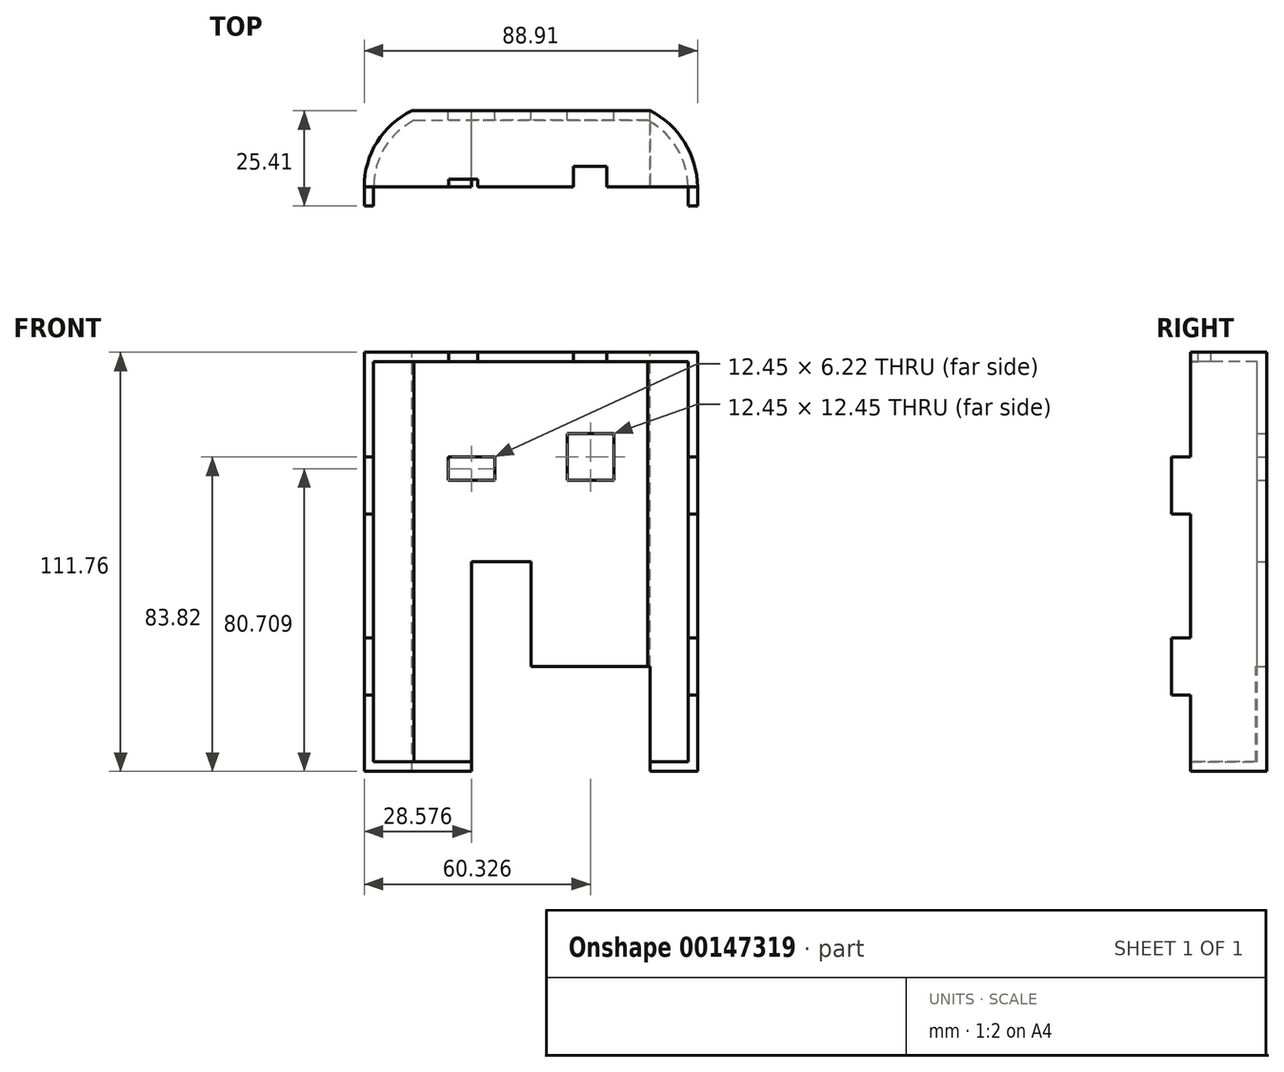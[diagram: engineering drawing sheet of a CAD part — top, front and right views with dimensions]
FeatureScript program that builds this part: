
annotation { "Feature Type Name" : "Feature", "Feature Type Description" : "" }
export const myFeature = defineFeature(function(context is Context, id is Id, definition is map)
    precondition{}
    {
        {
            var Q0;
            Q0=qCreatedBy(makeId("Top.planeOp"),FACE);
            var sketch = newSketch(context, id + "F0", { "sketchPlane" : qUnion([Q0])});
            skLineSegment(sketch, "E0.bottom", {"start": v(-8.58, 19.44) * mm, "end": v(54.92, 19.44) * mm});
            skLineSegment(sketch, "E1", {"start": v(67.63, -0.89) * mm, "end": v(-21.28, -0.89) * mm});
            skArc(sketch, "E2", {"start": v(-8.58, 19.44) * mm, "mid": v(-17.85, 11.1) * mm, "end": v(-21.28, -0.89) * mm});
            skArc(sketch, "E3", {"start": v(67.63, -0.89) * mm, "mid": v(64.16, 11.08) * mm, "end": v(54.92, 19.44) * mm});
            skLineSegment(sketch, "E4", {"start": v(1.33, -0.88) * mm, "end": v(1.33, 1.2) * mm});
            skLineSegment(sketch, "E5", {"start": v(1.33, 1.2) * mm, "end": v(9.07, 1.2) * mm});
            skLineSegment(sketch, "E6", {"start": v(9.07, 1.2) * mm, "end": v(9.07, -0.89) * mm});
            skLineSegment(sketch, "E7", {"start": v(34.47, -0.89) * mm, "end": v(34.47, 4.57) * mm});
            skLineSegment(sketch, "E8", {"start": v(34.47, 4.57) * mm, "end": v(43.41, 4.57) * mm});
            skLineSegment(sketch, "E9", {"start": v(43.41, 4.57) * mm, "end": v(43.41, -0.89) * mm});
            skSolve(sketch);
        }
        {
            var Q0;
            Q0=makeQuery(id+"F0.imprint","IMPRINT",FACE,{"disambiguationData":[TD([[makeQuery(id+"F0.imprint","IMPRINT",EDGE,{"derivedFrom":sQuery(id+"F0.wireOp",EDGE,"E0.bottom")}),-1.0]])]});
            var Q1;
            {var subQ0=sQuery(id+"F0.wireOp",EDGE,"E7");Q1=makeQuery(id+"F0.imprint","IMPRINT",FACE,{"disambiguationData":[TD([[makeQuery(id+"F0.imprint","IMPRINT",EDGE,{"derivedFrom":subQ0}),-1.0]])]});}
            extrude(context, id + "F1", {"entities" : qUnion([Q0, Q1]), "oppositeDirection" : true, "depth" : 111.76 * mm});
        }
        {
            var Q0;
            Q0=makeQuery(id+"F1.opExtrude","SWEPT_FACE",FACE,{"disambiguationData":[OSD([sQuery(id+"F0.wireOp",EDGE,"E1")])]});
            shell(context, id + "F2", {"entities" : qUnion([Q0]), "thickness" : 2.54 * mm});
        }
        {
            var Q0;
            Q0=makeQuery(id+"F0.imprint","IMPRINT",FACE,{"disambiguationData":[TD([[makeQuery(id+"F0.imprint","IMPRINT",EDGE,{"derivedFrom":sQuery(id+"F0.wireOp",EDGE,"E0.bottom")}),-1.0]])]});
            var sketch = newSketch(context, id + "F3", { "sketchPlane" : qUnion([Q0])});
            skLineSegment(sketch, "E10.bottom", {"start": v(1.31, -0.89) * mm, "end": v(9.06, -0.89) * mm});
            skLineSegment(sketch, "E10.top", {"start": v(1.31, 1.2) * mm, "end": v(9.06, 1.2) * mm});
            skLineSegment(sketch, "E10.left", {"start": v(1.31, -0.89) * mm, "end": v(1.31, 1.2) * mm});
            skLineSegment(sketch, "E10.right", {"start": v(9.06, -0.89) * mm, "end": v(9.06, 1.2) * mm});
            skLineSegment(sketch, "E11.bottom", {"start": v(34.46, -0.88) * mm, "end": v(43.4, -0.88) * mm});
            skLineSegment(sketch, "E11.top", {"start": v(34.46, 4.58) * mm, "end": v(43.4, 4.58) * mm});
            skLineSegment(sketch, "E11.left", {"start": v(34.46, -0.88) * mm, "end": v(34.46, 4.58) * mm});
            skLineSegment(sketch, "E11.right", {"start": v(43.4, -0.88) * mm, "end": v(43.4, 4.58) * mm});
            skSolve(sketch);
        }
        {
            var Q0;
            {var subQ0=sQuery(id+"F3.wireOp",EDGE,"E10.top");Q0=makeQuery(id+"F3.imprint","IMPRINT",FACE,{"disambiguationData":[TD([[makeQuery(id+"F3.imprint","IMPRINT",EDGE,{"derivedFrom":subQ0}),-1.0]])]});}
            extrude(context, id + "F4", {"entities" : qUnion([Q0]), "operationType" : NewBodyOperationType.REMOVE, "oppositeDirection" : true, "depth" : 25.4 * mm});
        }
        {
            var Q0;
            {var subQ0=sQuery(id+"F0.wireOp",EDGE,"E7");Q0=makeQuery(id+"F0.imprint","IMPRINT",FACE,{"disambiguationData":[TD([[makeQuery(id+"F0.imprint","IMPRINT",EDGE,{"derivedFrom":subQ0}),-1.0]])]});}
            extrude(context, id + "F5", {"entities" : qUnion([Q0]), "operationType" : NewBodyOperationType.REMOVE, "oppositeDirection" : true, "depth" : 25.4 * mm});
        }
        {
            var Q0;
            Q0=makeQuery(id+"F1.opExtrude","CAP_FACE",FACE,{"disambiguationData":[OSD([sQuery(id+"F0.wireOp",EDGE,"E0.bottom"),sQuery(id+"F0.wireOp",EDGE,"E1"),sQuery(id+"F0.wireOp",EDGE,"E2"),sQuery(id+"F0.wireOp",EDGE,"E3")])],"isStart":false});
            var sketch = newSketch(context, id + "F6", { "sketchPlane" : qUnion([Q0])});
            skPoint(sketch, "E12", {"position": v(23.17, 0.89) * mm});
            skArc(sketch, "E13", {"start": v(17.33, 0.89) * mm, "mid": v(23.17, -4.96) * mm, "end": v(29.02, 0.89) * mm});
            skSolve(sketch);
        }
        {
            var Q0;
            {var subQ0=sQuery(id+"F6.wireOp",EDGE,"E13");Q0=makeQuery(id+"F6.imprint","IMPRINT",FACE,{"disambiguationData":[TD([[makeQuery(id+"F6.imprint","IMPRINT",EDGE,{"derivedFrom":subQ0}),1.0]])]});}
            extrude(context, id + "F7", {"entities" : qUnion([Q0]), "operationType" : NewBodyOperationType.REMOVE, "oppositeDirection" : true, "depth" : 25.4 * mm});
        }
        {
            var Q0;
            {var subQ0=sQuery(id+"F0.wireOp",EDGE,"E3");var subQ1=sQuery(id+"F0.wireOp",EDGE,"E2");var subQ2=sQuery(id+"F0.wireOp",EDGE,"E1");var subQ6=makeQuery(id+"F1.opExtrude","SWEPT_FACE",FACE,{"disambiguationData":[OSD([subQ0])]});Q0=makeQuery(id+"F7.boolean.opBoolean","SPLIT",FACE,{"disambiguationData":[TD([subQ6])],"derivedFrom":makeQuery(id+"F5.boolean.opBoolean","SPLIT",FACE,{"disambiguationData":[TD([makeQuery(id+"F1.opExtrude","SWEPT_FACE",FACE,{"disambiguationData":[OSD([subQ1])]})])],"derivedFrom":makeQuery(id+"F1.opExtrude","SWEPT_FACE",FACE,{"disambiguationData":[OSD([subQ2])]})})});}
            var sketch = newSketch(context, id + "F8", { "sketchPlane" : qUnion([Q0])});
            skLineSegment(sketch, "E14", {"start": v(67.63, 0) * mm, "end": v(67.63, -111.76) * mm});
            skLineSegment(sketch, "E15", {"start": v(67.63, -55.88) * mm, "end": v(67.63, 0) * mm});
            skLineSegment(sketch, "E16", {"start": v(67.63, -55.88) * mm, "end": v(67.63, -111.76) * mm});
            skLineSegment(sketch, "E17", {"start": v(67.63, -27.94) * mm, "end": v(65.09, -27.94) * mm});
            skLineSegment(sketch, "E18", {"start": v(67.63, -83.82) * mm, "end": v(65.09, -83.82) * mm});
            skLineSegment(sketch, "E19.top", {"start": v(67.63, -76.2) * mm, "end": v(65.09, -76.2) * mm});
            skLineSegment(sketch, "E19.left", {"start": v(67.63, -83.82) * mm, "end": v(67.63, -76.2) * mm});
            skLineSegment(sketch, "E19.right", {"start": v(65.09, -83.82) * mm, "end": v(65.09, -76.2) * mm});
            skLineSegment(sketch, "E20.top", {"start": v(67.63, -91.44) * mm, "end": v(65.09, -91.44) * mm});
            skLineSegment(sketch, "E20.left", {"start": v(67.63, -83.82) * mm, "end": v(67.63, -91.44) * mm});
            skLineSegment(sketch, "E20.right", {"start": v(65.09, -83.82) * mm, "end": v(65.09, -91.44) * mm});
            skLineSegment(sketch, "E21.top", {"start": v(67.63, -35.56) * mm, "end": v(65.09, -35.56) * mm});
            skLineSegment(sketch, "E21.left", {"start": v(67.63, -27.94) * mm, "end": v(67.63, -35.56) * mm});
            skLineSegment(sketch, "E21.right", {"start": v(65.09, -27.94) * mm, "end": v(65.09, -35.56) * mm});
            skLineSegment(sketch, "E22.top", {"start": v(67.63, -43.18) * mm, "end": v(65.09, -43.18) * mm});
            skLineSegment(sketch, "E22.left", {"start": v(67.63, -35.56) * mm, "end": v(67.63, -43.18) * mm});
            skLineSegment(sketch, "E22.right", {"start": v(65.09, -35.56) * mm, "end": v(65.09, -43.18) * mm});
            skSolve(sketch);
        }
        {
            var Q0;
            Q0=makeQuery(id+"F8.imprint","IMPRINT",FACE,{"disambiguationData":[TD([[makeQuery(id+"F8.imprint","IMPRINT",EDGE,{"derivedFrom":sQuery(id+"F8.wireOp",EDGE,"E17")}),1.0]])]});
            var Q1;
            Q1=makeQuery(id+"F8.imprint","IMPRINT",FACE,{"disambiguationData":[TD([[makeQuery(id+"F8.imprint","IMPRINT",EDGE,{"derivedFrom":sQuery(id+"F8.wireOp",EDGE,"E21.top")}),1.0]])]});
            var Q2;
            Q2=makeQuery(id+"F8.imprint","IMPRINT",FACE,{"disambiguationData":[TD([[makeQuery(id+"F8.imprint","IMPRINT",EDGE,{"derivedFrom":sQuery(id+"F8.wireOp",EDGE,"E19.top")}),1.0]])]});
            var Q3;
            Q3=makeQuery(id+"F8.imprint","IMPRINT",FACE,{"disambiguationData":[TD([[makeQuery(id+"F8.imprint","IMPRINT",EDGE,{"derivedFrom":sQuery(id+"F8.wireOp",EDGE,"E18")}),1.0]])]});
            extrude(context, id + "F9", {"entities" : qUnion([Q0, Q1, Q2, Q3]), "operationType" : NewBodyOperationType.ADD, "depth" : 5.08 * mm});
        }
        {
            var Q0;
            {var subQ1=sQuery(id+"F0.wireOp",EDGE,"E2");var subQ2=sQuery(id+"F0.wireOp",EDGE,"E1");var subQ6=makeQuery(id+"F1.opExtrude","SWEPT_FACE",FACE,{"disambiguationData":[OSD([subQ1])]});Q0=makeQuery(id+"F7.boolean.opBoolean","SPLIT",FACE,{"disambiguationData":[TD([subQ6])],"derivedFrom":makeQuery(id+"F5.boolean.opBoolean","SPLIT",FACE,{"disambiguationData":[TD([subQ6])],"derivedFrom":makeQuery(id+"F1.opExtrude","SWEPT_FACE",FACE,{"disambiguationData":[OSD([subQ2])]})})});}
            var sketch = newSketch(context, id + "F10", { "sketchPlane" : qUnion([Q0])});
            skLineSegment(sketch, "E23", {"start": v(-21.28, 0) * mm, "end": v(-21.28, -111.76) * mm});
            skLineSegment(sketch, "E24", {"start": v(-21.28, -111.76) * mm, "end": v(-21.28, -55.88) * mm});
            skLineSegment(sketch, "E25", {"start": v(-21.28, -55.88) * mm, "end": v(-21.28, 0) * mm});
            skLineSegment(sketch, "E26", {"start": v(-21.28, -27.94) * mm, "end": v(-18.74, -27.94) * mm});
            skPoint(sketch, "E26.endSnap0", {"position": v(-18.74, -55.88) * mm});
            skLineSegment(sketch, "E27", {"start": v(-21.28, -83.82) * mm, "end": v(-18.74, -83.82) * mm});
            skLineSegment(sketch, "E28.top", {"start": v(-21.28, -43.18) * mm, "end": v(-18.74, -43.18) * mm});
            skLineSegment(sketch, "E28.left", {"start": v(-21.28, -27.94) * mm, "end": v(-21.28, -43.18) * mm});
            skLineSegment(sketch, "E28.right", {"start": v(-18.74, -27.94) * mm, "end": v(-18.74, -43.18) * mm});
            skLineSegment(sketch, "E29.top", {"start": v(-21.28, -76.2) * mm, "end": v(-18.74, -76.2) * mm});
            skLineSegment(sketch, "E29.left", {"start": v(-21.28, -83.82) * mm, "end": v(-21.28, -76.2) * mm});
            skLineSegment(sketch, "E29.right", {"start": v(-18.74, -83.82) * mm, "end": v(-18.74, -76.2) * mm});
            skLineSegment(sketch, "E30.top", {"start": v(-21.28, -91.44) * mm, "end": v(-18.74, -91.44) * mm});
            skLineSegment(sketch, "E30.left", {"start": v(-21.28, -83.82) * mm, "end": v(-21.28, -91.44) * mm});
            skLineSegment(sketch, "E30.right", {"start": v(-18.74, -83.82) * mm, "end": v(-18.74, -91.44) * mm});
            skSolve(sketch);
        }
        {
            var Q0;
            Q0=makeQuery(id+"F10.imprint","IMPRINT",FACE,{"disambiguationData":[TD([[makeQuery(id+"F10.imprint","IMPRINT",EDGE,{"derivedFrom":sQuery(id+"F10.wireOp",EDGE,"E26")}),-1.0]])]});
            var Q1;
            Q1=makeQuery(id+"F10.imprint","IMPRINT",FACE,{"disambiguationData":[TD([[makeQuery(id+"F10.imprint","IMPRINT",EDGE,{"derivedFrom":sQuery(id+"F10.wireOp",EDGE,"E29.top")}),-1.0]])]});
            var Q2;
            Q2=makeQuery(id+"F10.imprint","IMPRINT",FACE,{"disambiguationData":[TD([[makeQuery(id+"F10.imprint","IMPRINT",EDGE,{"derivedFrom":sQuery(id+"F10.wireOp",EDGE,"E27")}),-1.0]])]});
            extrude(context, id + "F11", {"entities" : qUnion([Q0, Q1, Q2]), "operationType" : NewBodyOperationType.ADD, "depth" : 5.08 * mm});
        }
        {
            var Q0;
            Q0=makeQuery(id+"F1.opExtrude","SWEPT_FACE",FACE,{"disambiguationData":[OSD([sQuery(id+"F0.wireOp",EDGE,"E0.bottom")])]});
            var sketch = newSketch(context, id + "F12", { "sketchPlane" : qUnion([Q0])});
            skLineSegment(sketch, "E31", {"start": v(-23.17, 0) * mm, "end": v(-23.17, -111.76) * mm});
            skLineSegment(sketch, "E32", {"start": v(8.58, -55.88) * mm, "end": v(-54.92, -55.88) * mm});
            skLineSegment(sketch, "E33", {"start": v(8.58, -55.88) * mm, "end": v(8.58, 0) * mm});
            skLineSegment(sketch, "E34", {"start": v(8.58, 0) * mm, "end": v(-23.17, 0) * mm});
            skLineSegment(sketch, "E35", {"start": v(-23.17, 0) * mm, "end": v(-54.92, 0) * mm});
            skLineSegment(sketch, "E36", {"start": v(-54.92, 0) * mm, "end": v(-54.92, -55.88) * mm});
            skLineSegment(sketch, "E37", {"start": v(-54.92, -55.88) * mm, "end": v(-54.92, -111.76) * mm});
            skLineSegment(sketch, "E38", {"start": v(-54.92, -111.76) * mm, "end": v(-23.17, -111.76) * mm});
            skLineSegment(sketch, "E39", {"start": v(-23.17, -111.76) * mm, "end": v(8.58, -111.76) * mm});
            skLineSegment(sketch, "E40", {"start": v(8.58, -111.76) * mm, "end": v(8.58, -55.88) * mm});
            skLineSegment(sketch, "E41", {"start": v(8.58, -83.82) * mm, "end": v(-23.17, -83.82) * mm});
            skLineSegment(sketch, "E42", {"start": v(-23.17, -55.88) * mm, "end": v(8.58, -55.88) * mm});
            skLineSegment(sketch, "E43", {"start": v(-23.17, -55.88) * mm, "end": v(-54.92, -55.88) * mm});
            skLineSegment(sketch, "E44", {"start": v(-7.3, -55.88) * mm, "end": v(-7.3, -111.76) * mm});
            skLineSegment(sketch, "E45", {"start": v(-7.3, -55.88) * mm, "end": v(-7.3, 0) * mm});
            skLineSegment(sketch, "E46", {"start": v(8.58, -27.94) * mm, "end": v(-23.17, -27.94) * mm});
            skPoint(sketch, "E46.endSnap0", {"position": v(-7.3, -27.94) * mm});
            skLineSegment(sketch, "E47", {"start": v(-23.17, -27.94) * mm, "end": v(-54.92, -27.94) * mm});
            skLineSegment(sketch, "E48", {"start": v(-39.05, 0) * mm, "end": v(-39.05, -111.76) * mm});
            skLineSegment(sketch, "E49", {"start": v(-23.17, -83.82) * mm, "end": v(-54.92, -83.82) * mm});
            skCircle(sketch, "E50", {"center": v(-7.3, -83.82) * mm, "radius": 4.45 * mm});
            skCircle(sketch, "E51", {"center": v(-39.05, -83.82) * mm, "radius": 4.45 * mm});
            skLineSegment(sketch, "E52", {"start": v(-7.3, -27.94) * mm, "end": v(-7.3, -21.72) * mm});
            skLineSegment(sketch, "E53", {"start": v(-7.3, -21.72) * mm, "end": v(-1.07, -21.72) * mm});
            skLineSegment(sketch, "E54", {"start": v(-1.07, -21.72) * mm, "end": v(-1.07, -27.94) * mm});
            skLineSegment(sketch, "E55.bottom", {"start": v(-1.07, -21.72) * mm, "end": v(-13.52, -21.72) * mm});
            skLineSegment(sketch, "E55.top", {"start": v(-1.07, -34.16) * mm, "end": v(-13.52, -34.16) * mm});
            skLineSegment(sketch, "E55.left", {"start": v(-1.07, -21.72) * mm, "end": v(-1.07, -34.16) * mm});
            skLineSegment(sketch, "E55.right", {"start": v(-13.52, -21.72) * mm, "end": v(-13.52, -34.16) * mm});
            skLineSegment(sketch, "E56.MirrorCS", {"start": v(-45.27, -21.72) * mm, "end": v(-32.82, -21.72) * mm});
            skLineSegment(sketch, "E57.MirrorCS", {"start": v(-32.82, -21.72) * mm, "end": v(-32.82, -34.16) * mm});
            skLineSegment(sketch, "E58.MirrorCS", {"start": v(-45.27, -34.16) * mm, "end": v(-32.82, -34.16) * mm});
            skLineSegment(sketch, "E59.MirrorCS", {"start": v(-45.27, -21.72) * mm, "end": v(-45.27, -34.16) * mm});
            skSolve(sketch);
        }
        {
            var Q0;
            {var subQ0=sQuery(id+"F12.wireOp",EDGE,"E52");Q0=makeQuery(id+"F12.imprint","IMPRINT",FACE,{"disambiguationData":[TD([[makeQuery(id+"F12.imprint","IMPRINT",EDGE,{"derivedFrom":subQ0}),-1.0]])]});}
            var Q1;
            {var subQ0=sQuery(id+"F12.wireOp",EDGE,"E52");Q1=makeQuery(id+"F12.imprint","IMPRINT",FACE,{"disambiguationData":[TD([[makeQuery(id+"F12.imprint","IMPRINT",EDGE,{"derivedFrom":subQ0}),1.0]])]});}
            var Q2;
            {var subQ3=sQuery(id+"F12.wireOp",EDGE,"E55.top");var subQ5=sQuery(id+"F12.wireOp",EDGE,"E55.right");var subQ6=makeQuery(id+"F12.imprint","INTERSECT",VERTEX,{"derivedFrom":[subQ3,subQ5]});Q2=makeQuery(id+"F12.imprint","IMPRINT",FACE,{"disambiguationData":[TD([[makeQuery(id+"F12.imprint","IMPRINT",EDGE,{"disambiguationData":[TD([[subQ6,1.0]])],"derivedFrom":subQ3}),-1.0]])]});}
            var Q3;
            {var subQ3=sQuery(id+"F12.wireOp",EDGE,"E55.top");var subQ5=sQuery(id+"F12.wireOp",EDGE,"E55.left");var subQ7=makeQuery(id+"F12.imprint","INTERSECT",VERTEX,{"derivedFrom":[subQ3,subQ5]});Q3=makeQuery(id+"F12.imprint","IMPRINT",FACE,{"disambiguationData":[TD([[makeQuery(id+"F12.imprint","IMPRINT",EDGE,{"disambiguationData":[TD([[subQ7,-1.0]])],"derivedFrom":subQ3}),-1.0]])]});}
            var Q4;
            {var subQ0=sQuery(id+"F12.wireOp",EDGE,"E57.MirrorCS");var subQ1=sQuery(id+"F12.wireOp",EDGE,"E47");var subQ2=makeQuery(id+"F12.imprint","INTERSECT",VERTEX,{"derivedFrom":[subQ1,subQ0]});Q4=makeQuery(id+"F12.imprint","IMPRINT",FACE,{"disambiguationData":[TD([[makeQuery(id+"F12.imprint","IMPRINT",EDGE,{"disambiguationData":[TD([[subQ2,-1.0]])],"derivedFrom":subQ1}),-1.0]])]});}
            var Q5;
            {var subQ0=sQuery(id+"F12.wireOp",EDGE,"E48");var subQ1=sQuery(id+"F12.wireOp",EDGE,"E47");var subQ2=makeQuery(id+"F12.imprint","INTERSECT",VERTEX,{"derivedFrom":[subQ1,subQ0]});Q5=makeQuery(id+"F12.imprint","IMPRINT",FACE,{"disambiguationData":[TD([[makeQuery(id+"F12.imprint","IMPRINT",EDGE,{"disambiguationData":[TD([[subQ2,-1.0]])],"derivedFrom":subQ1}),-1.0]])]});}
            var Q6;
            {var subQ0=sQuery(id+"F12.wireOp",EDGE,"E48");var subQ1=sQuery(id+"F12.wireOp",EDGE,"E47");var subQ2=makeQuery(id+"F12.imprint","INTERSECT",VERTEX,{"derivedFrom":[subQ1,subQ0]});Q6=makeQuery(id+"F12.imprint","IMPRINT",FACE,{"disambiguationData":[TD([[makeQuery(id+"F12.imprint","IMPRINT",EDGE,{"disambiguationData":[TD([[subQ2,-1.0]])],"derivedFrom":subQ1}),1.0]])]});}
            var Q7;
            {var subQ0=sQuery(id+"F12.wireOp",EDGE,"E57.MirrorCS");var subQ1=sQuery(id+"F12.wireOp",EDGE,"E47");var subQ2=makeQuery(id+"F12.imprint","INTERSECT",VERTEX,{"derivedFrom":[subQ1,subQ0]});Q7=makeQuery(id+"F12.imprint","IMPRINT",FACE,{"disambiguationData":[TD([[makeQuery(id+"F12.imprint","IMPRINT",EDGE,{"disambiguationData":[TD([[subQ2,-1.0]])],"derivedFrom":subQ1}),1.0]])]});}
            var Q8;
            {var subQ0=sQuery(id+"F12.wireOp",EDGE,"E51");var subQ1=sQuery(id+"F12.wireOp",EDGE,"E48");var subQ2=makeQuery(id+"F12.imprint","INTERSECT",VERTEX,{"disambiguationData":[OD(0.0)],"derivedFrom":[subQ1,subQ0]});Q8=makeQuery(id+"F12.imprint","IMPRINT",FACE,{"disambiguationData":[TD([[makeQuery(id+"F12.imprint","IMPRINT",EDGE,{"disambiguationData":[TD([[subQ2,-1.0]])],"derivedFrom":subQ1}),-1.0]])]});}
            var Q9;
            {var subQ0=sQuery(id+"F12.wireOp",EDGE,"E49");var subQ1=sQuery(id+"F12.wireOp",EDGE,"E48");var subQ2=makeQuery(id+"F12.imprint","INTERSECT",VERTEX,{"derivedFrom":[subQ1,subQ0]});Q9=makeQuery(id+"F12.imprint","IMPRINT",FACE,{"disambiguationData":[TD([[makeQuery(id+"F12.imprint","IMPRINT",EDGE,{"disambiguationData":[TD([[subQ2,-1.0]])],"derivedFrom":subQ1}),-1.0]])]});}
            var Q10;
            {var subQ0=sQuery(id+"F12.wireOp",EDGE,"E49");var subQ1=sQuery(id+"F12.wireOp",EDGE,"E48");var subQ2=makeQuery(id+"F12.imprint","INTERSECT",VERTEX,{"derivedFrom":[subQ1,subQ0]});Q10=makeQuery(id+"F12.imprint","IMPRINT",FACE,{"disambiguationData":[TD([[makeQuery(id+"F12.imprint","IMPRINT",EDGE,{"disambiguationData":[TD([[subQ2,-1.0]])],"derivedFrom":subQ1}),1.0]])]});}
            var Q11;
            {var subQ0=sQuery(id+"F12.wireOp",EDGE,"E51");var subQ1=sQuery(id+"F12.wireOp",EDGE,"E48");var subQ2=makeQuery(id+"F12.imprint","INTERSECT",VERTEX,{"disambiguationData":[OD(0.0)],"derivedFrom":[subQ1,subQ0]});Q11=makeQuery(id+"F12.imprint","IMPRINT",FACE,{"disambiguationData":[TD([[makeQuery(id+"F12.imprint","IMPRINT",EDGE,{"disambiguationData":[TD([[subQ2,-1.0]])],"derivedFrom":subQ1}),1.0]])]});}
            var Q12;
            {var subQ0=sQuery(id+"F12.wireOp",EDGE,"E44");var subQ1=sQuery(id+"F12.wireOp",EDGE,"E41");var subQ2=makeQuery(id+"F12.imprint","INTERSECT",VERTEX,{"derivedFrom":[subQ1,subQ0]});Q12=makeQuery(id+"F12.imprint","IMPRINT",FACE,{"disambiguationData":[TD([[makeQuery(id+"F12.imprint","IMPRINT",EDGE,{"disambiguationData":[TD([[subQ2,-1.0]])],"derivedFrom":subQ1}),-1.0]])]});}
            var Q13;
            {var subQ0=sQuery(id+"F12.wireOp",EDGE,"E44");var subQ1=sQuery(id+"F12.wireOp",EDGE,"E41");var subQ2=makeQuery(id+"F12.imprint","INTERSECT",VERTEX,{"derivedFrom":[subQ1,subQ0]});Q13=makeQuery(id+"F12.imprint","IMPRINT",FACE,{"disambiguationData":[TD([[makeQuery(id+"F12.imprint","IMPRINT",EDGE,{"disambiguationData":[TD([[subQ2,-1.0]])],"derivedFrom":subQ1}),1.0]])]});}
            var Q14;
            {var subQ0=sQuery(id+"F12.wireOp",EDGE,"E50");var subQ1=sQuery(id+"F12.wireOp",EDGE,"E41");var subQ2=makeQuery(id+"F12.imprint","INTERSECT",VERTEX,{"disambiguationData":[OD(0.0)],"derivedFrom":[subQ1,subQ0]});Q14=makeQuery(id+"F12.imprint","IMPRINT",FACE,{"disambiguationData":[TD([[makeQuery(id+"F12.imprint","IMPRINT",EDGE,{"disambiguationData":[TD([[subQ2,-1.0]])],"derivedFrom":subQ1}),1.0]])]});}
            var Q15;
            {var subQ0=sQuery(id+"F12.wireOp",EDGE,"E50");var subQ1=sQuery(id+"F12.wireOp",EDGE,"E41");var subQ2=makeQuery(id+"F12.imprint","INTERSECT",VERTEX,{"disambiguationData":[OD(0.0)],"derivedFrom":[subQ1,subQ0]});Q15=makeQuery(id+"F12.imprint","IMPRINT",FACE,{"disambiguationData":[TD([[makeQuery(id+"F12.imprint","IMPRINT",EDGE,{"disambiguationData":[TD([[subQ2,-1.0]])],"derivedFrom":subQ1}),-1.0]])]});}
            extrude(context, id + "F13", {"entities" : qUnion([Q0, Q1, Q2, Q3, Q4, Q5, Q6, Q7, Q8, Q9, Q10, Q11, Q12, Q13, Q14, Q15]), "operationType" : NewBodyOperationType.REMOVE, "oppositeDirection" : true, "depth" : 25.4 * mm});
        }
    });
